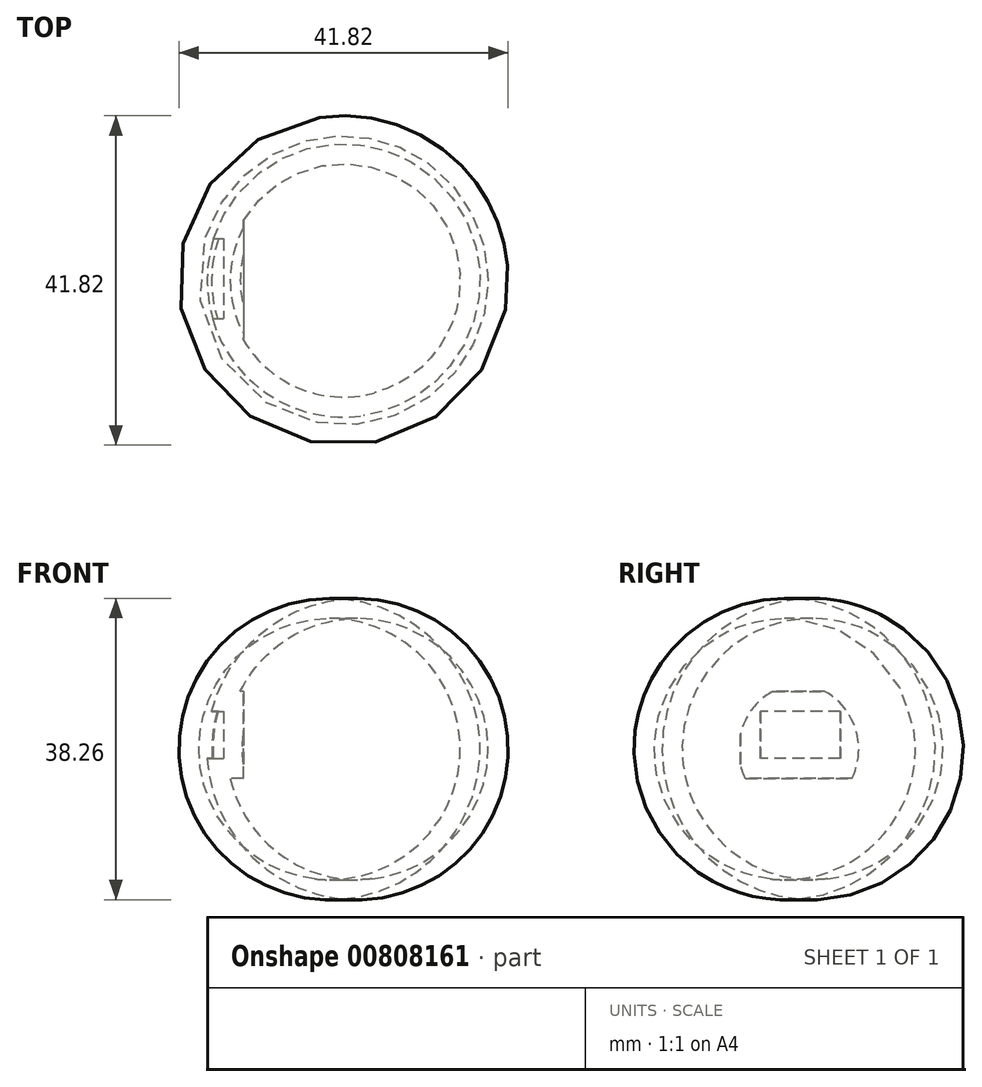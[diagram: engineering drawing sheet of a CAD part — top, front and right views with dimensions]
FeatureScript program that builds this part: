
annotation { "Feature Type Name" : "Feature", "Feature Type Description" : "" }
export const myFeature = defineFeature(function(context is Context, id is Id, definition is map)
    precondition{}
    {
        {
            var Q0;
            Q0=qCreatedBy(makeId("Right.planeOp"),FACE);
            var sketch = newSketch(context, id + "F0", { "sketchPlane" : qUnion([Q0])});
            skArc(sketch, "E0", {"start": v(0, 38.1) * mm, "mid": v(-17.35, 19.05) * mm, "end": v(0, 0) * mm});
            skLineSegment(sketch, "E1", {"start": v(0, 0) * mm, "end": v(0, 38.1) * mm});
            skSolve(sketch);
        }
        {
            var Q0;
            Q0=makeQuery(id+"F0.imprint","IMPRINT",FACE,{"disambiguationData":[TD([[makeQuery(id+"F0.imprint","IMPRINT",EDGE,{"derivedFrom":sQuery(id+"F0.wireOp",EDGE,"E0")}),1.0]])]});
            var Q1;
            Q1=sQuery(id+"F0.wireOp",EDGE,"E1");
            revolve(context, id + "F1", {"surfaceOperationType" : NewSurfaceOperationType.NEW, "entities" : qUnion([Q0]), "axis" : qUnion([Q1]), "revolveType" : RevolveType.FULL});
        }
        {
            var Q0;
            Q0=qCreatedBy(makeId("Right.planeOp"),FACE);
            cPlane(context, id + "F2", {"entities" : qUnion([Q0]), "cplaneType" : CPlaneType.OFFSET, "offset" : 15.24 * mm, "oppositeDirection" : true, "width" : 152.4 * mm, "height" : 152.4 * mm});
        }
        {
            var Q0;
            Q0=qCreatedBy(id+"F2.planeOp",FACE);
            var sketch = newSketch(context, id + "F3", { "sketchPlane" : qUnion([Q0])});
            skLineSegment(sketch, "E2.bottom", {"start": v(5.3, 23.83) * mm, "end": v(-4.86, 23.83) * mm});
            skLineSegment(sketch, "E2.top", {"start": v(5.3, 17.87) * mm, "end": v(-4.86, 17.87) * mm});
            skLineSegment(sketch, "E2.left", {"start": v(5.3, 23.83) * mm, "end": v(5.3, 17.87) * mm});
            skLineSegment(sketch, "E2.right", {"start": v(-4.86, 23.83) * mm, "end": v(-4.86, 17.87) * mm});
            skSolve(sketch);
        }
        {
            var Q0;
            Q0 = qSketchRegion(id + "F3", true);
            extrude(context, id + "F4", {"entities" : qUnion([Q0]), "operationType" : NewBodyOperationType.REMOVE, "endBound" : BoundingType.UP_TO_NEXT, "oppositeDirection" : true, "depth" : 25.4 * mm, "offsetDistance" : 25.4 * mm});
        }
        {
            var Q0;
            Q0=makeQuery(id+"F4.boolean.opBoolean","COPY",FACE,{"derivedFrom":makeQuery(id+"F4.opExtrude","CAP_FACE",FACE,{"disambiguationData":[OSD([sQuery(id+"F3.wireOp",EDGE,"E2.bottom"),sQuery(id+"F3.wireOp",EDGE,"E2.top"),sQuery(id+"F3.wireOp",EDGE,"E2.left"),sQuery(id+"F3.wireOp",EDGE,"E2.right")])],"isStart":true})});
            var Q1;
            Q1=makeQuery(id+"F1.opRevolve","SWEPT_BODY",BODY,{"disambiguationData":[OSD([sQuery(id+"F0.wireOp",EDGE,"E0"),sQuery(id+"F0.wireOp",EDGE,"E1")])]});
            shell(context, id + "F5", {"isHollow" : true, "entities" : qUnion([Q0]), "parts" : qUnion([Q1]), "thickness" : 2.54 * mm});
        }
    });
